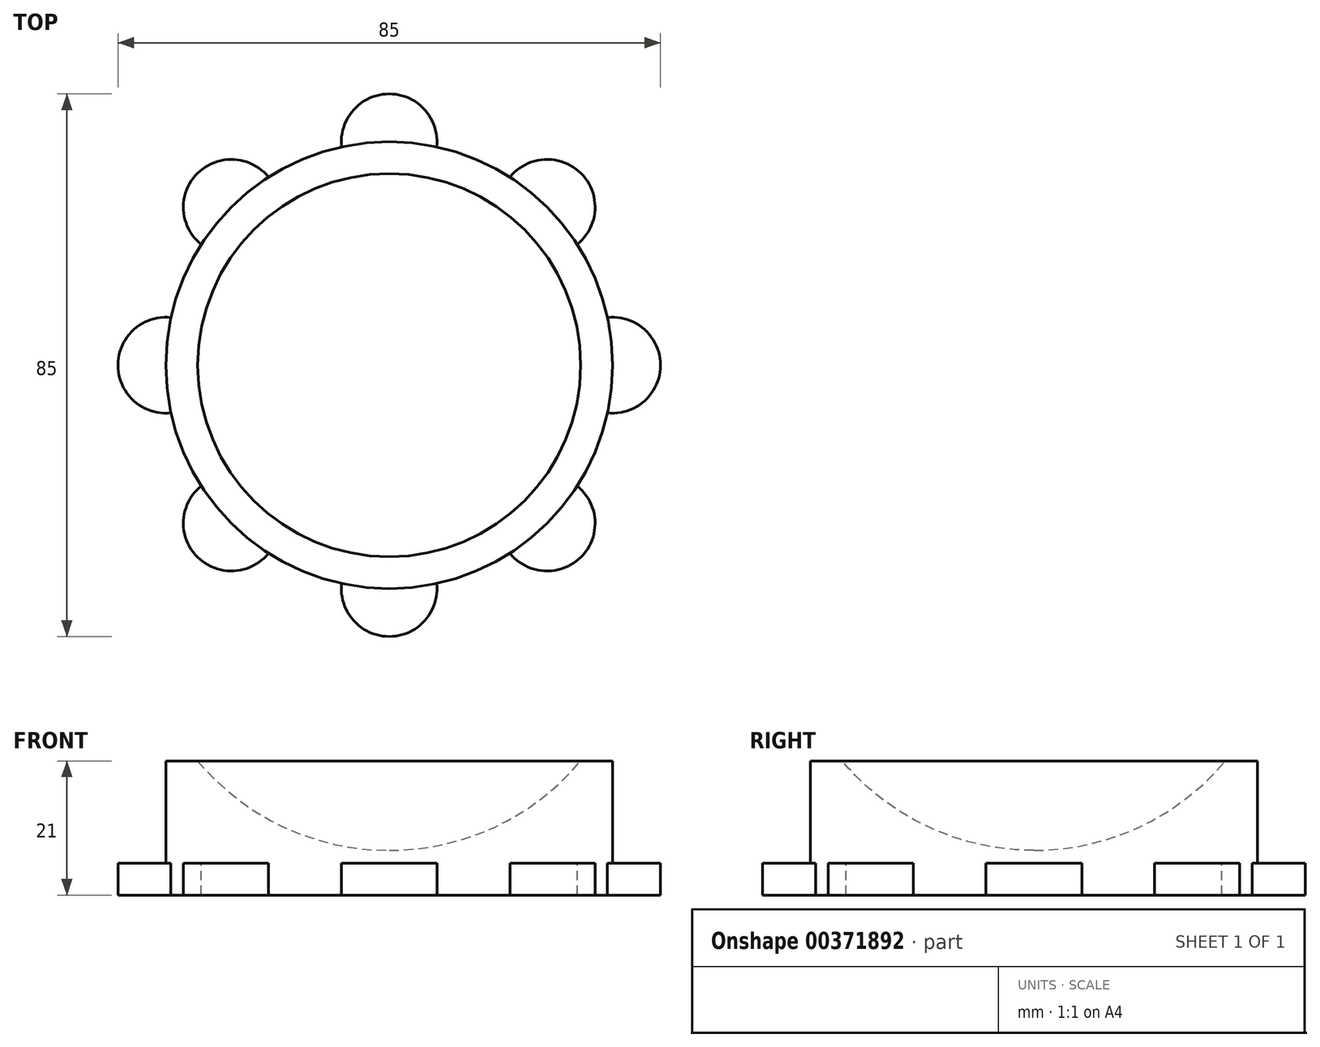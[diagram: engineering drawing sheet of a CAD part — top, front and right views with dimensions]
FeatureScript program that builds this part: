
annotation { "Feature Type Name" : "Feature", "Feature Type Description" : "" }
export const myFeature = defineFeature(function(context is Context, id is Id, definition is map)
    precondition{}
    {
        {
            var Q0;
            Q0=qCreatedBy(makeId("Right.planeOp"),FACE);
            var sketch = newSketch(context, id + "F0", { "sketchPlane" : qUnion([Q0])});
            skLineSegment(sketch, "E0", {"start": v(0, -16) * mm, "end": v(35, -16) * mm});
            skLineSegment(sketch, "E1", {"start": v(35, -16) * mm, "end": v(35, 0) * mm});
            skLineSegment(sketch, "E2", {"start": v(35, 0) * mm, "end": v(30, 0) * mm});
            skLineSegment(sketch, "E3", {"start": v(0, -16) * mm, "end": v(0, -14) * mm});
            skArc(sketch, "E4", {"start": v(30, 0) * mm, "mid": v(16.55, -10.33) * mm, "end": v(0, -14) * mm});
            skLineSegment(sketch, "E5", {"start": v(0, 12.27) * mm, "end": v(0, -16) * mm});
            skSolve(sketch);
        }
        {
            var Q0;
            Q0 = qSketchRegion(id + "F0", true);
            var Q1;
            Q1=sQuery(id+"F0.wireOp",EDGE,"E5");
            revolve(context, id + "F1", {"entities" : qUnion([Q0]), "axis" : qUnion([Q1]), "revolveType" : RevolveType.FULL});
        }
        {
            var Q0;
            Q0=makeQuery(id+"F1.opRevolve","SWEPT_FACE",FACE,{"disambiguationData":[OSD([sQuery(id+"F0.wireOp",EDGE,"E0")])]});
            var sketch = newSketch(context, id + "F2", { "sketchPlane" : qUnion([Q0])});
            skArc(sketch, "E6", {"start": v(-29.45, 18.9) * mm, "mid": v(-32.34, 13.4) * mm, "end": v(-34.2, 7.46) * mm});
            skArc(sketch, "E7", {"start": v(34.2, -7.46) * mm, "mid": v(42.5, 0) * mm, "end": v(34.2, 7.46) * mm});
            skArc(sketch, "E8", {"start": v(-7.46, -34.2) * mm, "mid": v(0, -42.5) * mm, "end": v(7.46, -34.2) * mm});
            skArc(sketch, "E9", {"start": v(-34.2, 7.46) * mm, "mid": v(-42.5, 0) * mm, "end": v(-34.2, -7.46) * mm});
            skArc(sketch, "E10", {"start": v(7.46, 34.2) * mm, "mid": v(0, 42.5) * mm, "end": v(-7.46, 34.2) * mm});
            skLineSegment(sketch, "E11", {"start": v(-28, 28) * mm, "end": v(0, 0) * mm});
            skLineSegment(sketch, "E12", {"start": v(-28, 28) * mm, "end": v(-28, 0) * mm});
            skLineSegment(sketch, "E13", {"start": v(-28, 0) * mm, "end": v(0, 0) * mm});
            skArc(sketch, "E14", {"start": v(-18.9, 29.45) * mm, "mid": v(-30.05, 30.05) * mm, "end": v(-29.45, 18.9) * mm});
            skLineSegment(sketch, "E15", {"start": v(0, 0) * mm, "end": v(68.36, -68.36) * mm});
            skArc(sketch, "E16", {"start": v(18.9, -29.45) * mm, "mid": v(30.05, -30.05) * mm, "end": v(29.45, -18.9) * mm});
            skLineSegment(sketch, "E17", {"start": v(0, 0) * mm, "end": v(50.25, 50.25) * mm});
            skLineSegment(sketch, "E18", {"start": v(0, 0) * mm, "end": v(-40.69, -40.69) * mm});
            skArc(sketch, "E19", {"start": v(29.45, 18.9) * mm, "mid": v(30.05, 30.05) * mm, "end": v(18.9, 29.45) * mm});
            skArc(sketch, "E20", {"start": v(-29.45, -18.9) * mm, "mid": v(-30.05, -30.05) * mm, "end": v(-18.9, -29.45) * mm});
            skArc(sketch, "E21.trimOffspring", {"start": v(-7.46, 34.2) * mm, "mid": v(-13.4, 32.34) * mm, "end": v(-18.9, 29.45) * mm});
            skArc(sketch, "E22.trimOffspring", {"start": v(18.9, 29.45) * mm, "mid": v(13.4, 32.34) * mm, "end": v(7.46, 34.2) * mm});
            skArc(sketch, "E23.trimOffspring", {"start": v(-34.2, -7.46) * mm, "mid": v(-32.34, -13.4) * mm, "end": v(-29.45, -18.9) * mm});
            skArc(sketch, "E24.trimOffspring", {"start": v(-18.9, -29.45) * mm, "mid": v(-13.4, -32.34) * mm, "end": v(-7.46, -34.2) * mm});
            skArc(sketch, "E25.trimOffspring", {"start": v(7.46, -34.2) * mm, "mid": v(13.4, -32.34) * mm, "end": v(18.9, -29.45) * mm});
            skArc(sketch, "E26.trimOffspring", {"start": v(29.45, -18.9) * mm, "mid": v(32.34, -13.4) * mm, "end": v(34.2, -7.46) * mm});
            skArc(sketch, "E27.trimOffspring", {"start": v(34.2, 7.46) * mm, "mid": v(32.34, 13.4) * mm, "end": v(29.45, 18.9) * mm});
            skSolve(sketch);
        }
        {
            var Q0;
            {var subQ0=sQuery(id+"F2.wireOp",EDGE,"E10");Q0=makeQuery(id+"F2.imprint","IMPRINT",FACE,{"disambiguationData":[TD([[makeQuery(id+"F2.imprint","IMPRINT",EDGE,{"derivedFrom":subQ0}),1.0]])]});}
            var Q1;
            {var subQ0=sQuery(id+"F2.wireOp",EDGE,"E19");var subQ1=sQuery(id+"F2.wireOp",EDGE,"E17");var subQ2=makeQuery(id+"F2.imprint","INTERSECT",VERTEX,{"derivedFrom":[subQ1,subQ0]});Q1=makeQuery(id+"F2.imprint","IMPRINT",FACE,{"disambiguationData":[TD([[makeQuery(id+"F2.imprint","IMPRINT",EDGE,{"disambiguationData":[TD([[subQ2,1.0]])],"derivedFrom":subQ1}),-1.0]])]});}
            var Q2;
            {var subQ0=sQuery(id+"F2.wireOp",EDGE,"E19");var subQ1=sQuery(id+"F2.wireOp",EDGE,"E17");var subQ2=makeQuery(id+"F2.imprint","INTERSECT",VERTEX,{"derivedFrom":[subQ1,subQ0]});Q2=makeQuery(id+"F2.imprint","IMPRINT",FACE,{"disambiguationData":[TD([[makeQuery(id+"F2.imprint","IMPRINT",EDGE,{"disambiguationData":[TD([[subQ2,1.0]])],"derivedFrom":subQ1}),1.0]])]});}
            var Q3;
            {var subQ0=sQuery(id+"F2.wireOp",EDGE,"E7");Q3=makeQuery(id+"F2.imprint","IMPRINT",FACE,{"disambiguationData":[TD([[makeQuery(id+"F2.imprint","IMPRINT",EDGE,{"derivedFrom":subQ0}),1.0]])]});}
            var Q4;
            {var subQ0=sQuery(id+"F2.wireOp",EDGE,"E16");var subQ1=sQuery(id+"F2.wireOp",EDGE,"E15");var subQ2=makeQuery(id+"F2.imprint","INTERSECT",VERTEX,{"derivedFrom":[subQ1,subQ0]});Q4=makeQuery(id+"F2.imprint","IMPRINT",FACE,{"disambiguationData":[TD([[makeQuery(id+"F2.imprint","IMPRINT",EDGE,{"disambiguationData":[TD([[subQ2,1.0]])],"derivedFrom":subQ1}),1.0]])]});}
            var Q5;
            {var subQ0=sQuery(id+"F2.wireOp",EDGE,"E16");var subQ1=sQuery(id+"F2.wireOp",EDGE,"E15");var subQ2=makeQuery(id+"F2.imprint","INTERSECT",VERTEX,{"derivedFrom":[subQ1,subQ0]});Q5=makeQuery(id+"F2.imprint","IMPRINT",FACE,{"disambiguationData":[TD([[makeQuery(id+"F2.imprint","IMPRINT",EDGE,{"disambiguationData":[TD([[subQ2,1.0]])],"derivedFrom":subQ1}),-1.0]])]});}
            var Q6;
            {var subQ0=sQuery(id+"F2.wireOp",EDGE,"E8");Q6=makeQuery(id+"F2.imprint","IMPRINT",FACE,{"disambiguationData":[TD([[makeQuery(id+"F2.imprint","IMPRINT",EDGE,{"derivedFrom":subQ0}),1.0]])]});}
            var Q7;
            {var subQ0=sQuery(id+"F2.wireOp",EDGE,"E20");var subQ1=sQuery(id+"F2.wireOp",EDGE,"E18");var subQ2=makeQuery(id+"F2.imprint","INTERSECT",VERTEX,{"derivedFrom":[subQ1,subQ0]});Q7=makeQuery(id+"F2.imprint","IMPRINT",FACE,{"disambiguationData":[TD([[makeQuery(id+"F2.imprint","IMPRINT",EDGE,{"disambiguationData":[TD([[subQ2,1.0]])],"derivedFrom":subQ1}),1.0]])]});}
            var Q8;
            {var subQ0=sQuery(id+"F2.wireOp",EDGE,"E20");var subQ1=sQuery(id+"F2.wireOp",EDGE,"E18");var subQ2=makeQuery(id+"F2.imprint","INTERSECT",VERTEX,{"derivedFrom":[subQ1,subQ0]});Q8=makeQuery(id+"F2.imprint","IMPRINT",FACE,{"disambiguationData":[TD([[makeQuery(id+"F2.imprint","IMPRINT",EDGE,{"disambiguationData":[TD([[subQ2,1.0]])],"derivedFrom":subQ1}),-1.0]])]});}
            var Q9;
            {var subQ0=sQuery(id+"F2.wireOp",EDGE,"E9");Q9=makeQuery(id+"F2.imprint","IMPRINT",FACE,{"disambiguationData":[TD([[makeQuery(id+"F2.imprint","IMPRINT",EDGE,{"derivedFrom":subQ0}),1.0]])]});}
            var Q10;
            {var subQ0=sQuery(id+"F2.wireOp",EDGE,"E14");Q10=makeQuery(id+"F2.imprint","IMPRINT",FACE,{"disambiguationData":[TD([[makeQuery(id+"F2.imprint","IMPRINT",EDGE,{"derivedFrom":subQ0}),1.0]])]});}
            var Q11;
            {var subQ1=sQuery(id+"F2.wireOp",EDGE,"E21.trimOffspring");Q11=makeQuery(id+"F2.imprint","IMPRINT",FACE,{"disambiguationData":[TD([[makeQuery(id+"F2.imprint","IMPRINT",EDGE,{"derivedFrom":subQ1}),-1.0]])]});}
            var Q12;
            {var subQ1=sQuery(id+"F2.wireOp",EDGE,"E26.trimOffspring");Q12=makeQuery(id+"F2.imprint","IMPRINT",FACE,{"disambiguationData":[TD([[makeQuery(id+"F2.imprint","IMPRINT",EDGE,{"derivedFrom":subQ1}),-1.0]])]});}
            var Q13;
            {var subQ6=sQuery(id+"F2.wireOp",EDGE,"E24.trimOffspring");Q13=makeQuery(id+"F2.imprint","IMPRINT",FACE,{"disambiguationData":[TD([[makeQuery(id+"F2.imprint","IMPRINT",EDGE,{"derivedFrom":subQ6}),-1.0]])]});}
            var Q14;
            {var subQ7=sQuery(id+"F2.wireOp",EDGE,"E6");Q14=makeQuery(id+"F2.imprint","IMPRINT",FACE,{"disambiguationData":[TD([[makeQuery(id+"F2.imprint","IMPRINT",EDGE,{"derivedFrom":subQ7}),-1.0]])]});}
            var Q15;
            {var subQ0=sQuery(id+"F2.wireOp",EDGE,"E13");Q15=makeQuery(id+"F2.imprint","IMPRINT",FACE,{"disambiguationData":[TD([[makeQuery(id+"F2.imprint","IMPRINT",EDGE,{"derivedFrom":subQ0}),1.0]])]});}
            var Q16;
            {var subQ0=sQuery(id+"F2.wireOp",EDGE,"E12");var subQ1=sQuery(id+"F2.wireOp",EDGE,"E11");var subQ2=makeQuery(id+"F2.imprint","INTERSECT",VERTEX,{"derivedFrom":[subQ1,subQ0]});Q16=makeQuery(id+"F2.imprint","IMPRINT",FACE,{"disambiguationData":[TD([[makeQuery(id+"F2.imprint","IMPRINT",EDGE,{"disambiguationData":[TD([[subQ2,-1.0]])],"derivedFrom":subQ1}),-1.0]])]});}
            extrude(context, id + "F3", {"entities" : qUnion([Q0, Q1, Q2, Q3, Q4, Q5, Q6, Q7, Q8, Q9, Q10, Q11, Q12, Q13, Q14, Q15, Q16]), "operationType" : NewBodyOperationType.ADD, "depth" : 5 * mm});
        }
    });
